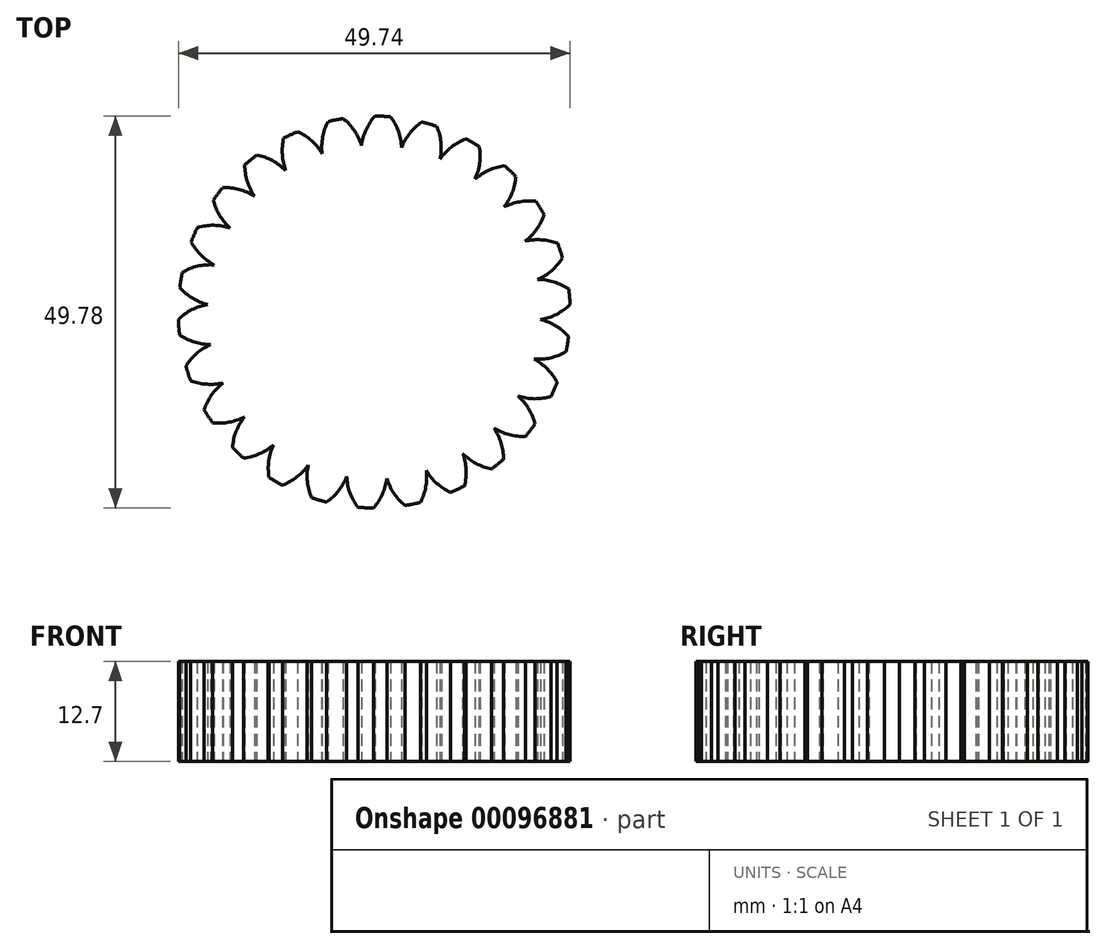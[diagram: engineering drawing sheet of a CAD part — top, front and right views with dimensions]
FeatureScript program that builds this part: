
annotation { "Feature Type Name" : "Feature", "Feature Type Description" : "" }
export const myFeature = defineFeature(function(context is Context, id is Id, definition is map)
    precondition{}
    {
        {
            var Q0;
            Q0=qCreatedBy(makeId("Top.planeOp"),FACE);
            var sketch = newSketch(context, id + "F0", { "sketchPlane" : qUnion([Q0])});
            skCircle(sketch, "E0", {"center": v(0, 0) * mm, "radius": 25.4 * mm, "construction": true});
            skCircle(sketch, "E1", {"center": v(0, 0) * mm, "radius": 24.9 * mm});
            skCircle(sketch, "E2", {"center": v(0, 0) * mm, "radius": 22.13 * mm, "construction": true});
            skCircle(sketch, "E3", {"center": v(0, 0) * mm, "radius": 20.9 * mm, "construction": true});
            skLineSegment(sketch, "E4", {"start": v(0, 20.9) * mm, "end": v(0, 25.4) * mm, "construction": true});
            skLineSegment(sketch, "E5", {"start": v(-6.36, 24.6) * mm, "end": v(-5.23, 20.23) * mm, "construction": true});
            skLineSegment(sketch, "E6", {"start": v(-5.23, 20.23) * mm, "end": v(0, 22.13) * mm, "construction": true});
            skLineSegment(sketch, "E7", {"start": v(-13.83, 20.7) * mm, "end": v(-14.11, 21.12) * mm});
            skLineSegment(sketch, "E8", {"start": v(0, 22.13) * mm, "end": v(6.63, 24.52) * mm, "construction": true});
            skLineSegment(sketch, "E9", {"start": v(10.24, 18.22) * mm, "end": v(3.9, 21.78) * mm, "construction": true});
            skCircle(sketch, "E10", {"center": v(10.24, 18.22) * mm, "radius": 7.26 * mm});
            skLineSegment(sketch, "E11", {"start": v(3.9, 21.78) * mm, "end": v(4.4, 24.5) * mm, "construction": true});
            skLineSegment(sketch, "E12", {"start": v(15.28, 19.65) * mm, "end": v(13.58, 17.47) * mm, "construction": true});
            skLineSegment(sketch, "E13", {"start": v(10.13, 22.74) * mm, "end": v(9, 20.21) * mm, "construction": true});
            skLineSegment(sketch, "E14", {"start": v(3.9, 21.78) * mm, "end": v(10.13, 22.74) * mm, "construction": true});
            skLineSegment(sketch, "E15", {"start": v(13.58, 17.47) * mm, "end": v(10.13, 22.74) * mm, "construction": true});
            skCircle(sketch, "E16", {"center": v(0, 0) * mm, "radius": 20.5 * mm});
            skLineSegment(sketch, "E17", {"start": v(5.68, 19.55) * mm, "end": v(3.26, 20.25) * mm, "construction": true});
            skLineSegment(sketch, "E18", {"start": v(9, 20.21) * mm, "end": v(8.5, 20.25) * mm});
            skLineSegment(sketch, "E19", {"start": v(8.5, 20.25) * mm, "end": v(1.77, 20.83) * mm, "construction": true});
            skCircle(sketch, "E20", {"center": v(1.77, 20.83) * mm, "radius": 6.75 * mm});
            skLineSegment(sketch, "E21", {"start": v(5.68, 19.55) * mm, "end": v(7.21, 24.82) * mm, "construction": true});
            skLineSegment(sketch, "E22", {"start": v(9, 20.21) * mm, "end": v(3.9, 21.78) * mm, "construction": true});
            skSolve(sketch);
        }
        {
            var Q0;
            {var subQ0=sQuery(id+"F0.wireOp",EDGE,"E20");var subQ3=sQuery(id+"F0.wireOp",EDGE,"E10");var subQ4=makeQuery(id+"F0.imprint","INTERSECT",VERTEX,{"disambiguationData":[OD(1.0)],"derivedFrom":[subQ3,subQ0]});Q0=makeQuery(id+"F0.imprint","IMPRINT",FACE,{"disambiguationData":[TD([[makeQuery(id+"F0.imprint","IMPRINT",EDGE,{"disambiguationData":[TD([[subQ4,-1.0]])],"derivedFrom":subQ3}),-1.0]])]});}
            var Q1;
            {var subQ1=sQuery(id+"F0.wireOp",EDGE,"E16");var subQ3=sQuery(id+"F0.wireOp",EDGE,"E10");var subQ5=makeQuery(id+"F0.imprint","INTERSECT",VERTEX,{"disambiguationData":[OD(0.0)],"derivedFrom":[subQ3,subQ1]});Q1=makeQuery(id+"F0.imprint","IMPRINT",FACE,{"disambiguationData":[TD([[makeQuery(id+"F0.imprint","IMPRINT",EDGE,{"disambiguationData":[TD([[subQ5,-1.0]])],"derivedFrom":subQ3}),1.0]])]});}
            var Q2;
            {var subQ1=sQuery(id+"F0.wireOp",EDGE,"E16");var subQ3=sQuery(id+"F0.wireOp",EDGE,"E10");var subQ5=makeQuery(id+"F0.imprint","INTERSECT",VERTEX,{"disambiguationData":[OD(0.0)],"derivedFrom":[subQ3,subQ1]});Q2=makeQuery(id+"F0.imprint","IMPRINT",FACE,{"disambiguationData":[TD([[makeQuery(id+"F0.imprint","IMPRINT",EDGE,{"disambiguationData":[TD([[subQ5,-1.0]])],"derivedFrom":subQ3}),-1.0]])]});}
            var Q3;
            {var subQ0=sQuery(id+"F0.wireOp",EDGE,"E20");var subQ3=makeQuery(id+"F0.imprint","IMPRINT",VERTEX,{"derivedFrom":subQ0});Q3=makeQuery(id+"F0.imprint","IMPRINT",FACE,{"disambiguationData":[TD([[makeQuery(id+"F0.imprint","IMPRINT",EDGE,{"disambiguationData":[TD([[subQ3,-1.0]])],"derivedFrom":subQ0}),1.0]])]});}
            extrude(context, id + "F1", {"entities" : qUnion([Q0, Q1, Q2, Q3]), "depth" : 12.7 * mm});
        }
        {
            var Q0;
            Q0=makeQuery(id+"F1.opExtrude","SWEPT_BODY",BODY,{"disambiguationData":[OSD([sQuery(id+"F0.wireOp",EDGE,"E1"),sQuery(id+"F0.wireOp",EDGE,"E10"),sQuery(id+"F0.wireOp",EDGE,"E16"),sQuery(id+"F0.wireOp",EDGE,"E20")])]});
            var Q1;
            Q1=makeQuery(id+"F1.opExtrude","CAP_EDGE",EDGE,{"disambiguationData":[OSD([sQuery(id+"F0.wireOp",EDGE,"E16")])],"isStart":false});
            circularPattern(context, id + "F2", {"operationType" : NewBodyOperationType.ADD, "entities" : qUnion([Q0]), "axis" : qUnion([Q1]), "angle" : 360 * degree, "instanceCount" : 26, "equalSpace" : true});
        }
    });
